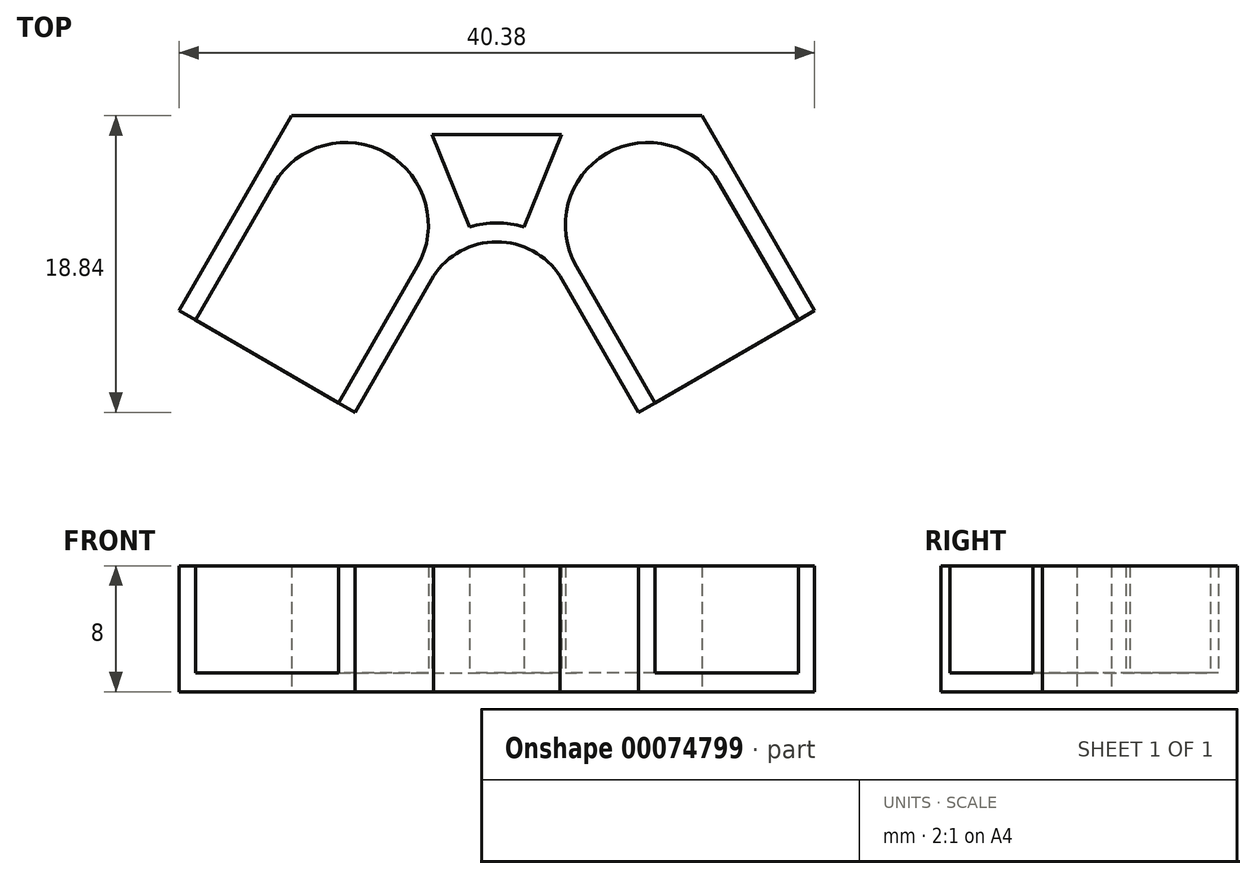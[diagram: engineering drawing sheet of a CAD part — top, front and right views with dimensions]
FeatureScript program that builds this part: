
annotation { "Feature Type Name" : "Feature", "Feature Type Description" : "" }
export const myFeature = defineFeature(function(context is Context, id is Id, definition is map)
    precondition{}
    {
        {
            var Q0;
            Q0=qCreatedBy(makeId("Top.planeOp"),FACE);
            var sketch = newSketch(context, id + "F0", { "sketchPlane" : qUnion([Q0])});
            skLineSegment(sketch, "E0", {"start": v(0, 33.26) * mm, "end": v(-19.2, 0) * mm, "construction": true});
            skLineSegment(sketch, "E1", {"start": v(-19.2, 0) * mm, "end": v(19.2, 0) * mm, "construction": true});
            skLineSegment(sketch, "E2", {"start": v(19.2, 0) * mm, "end": v(0, 33.26) * mm, "construction": true});
            skLineSegment(sketch, "E3", {"start": v(19.2, 0) * mm, "end": v(-5.05, 14) * mm, "construction": true});
            skLineSegment(sketch, "E4", {"start": v(0, 43.76) * mm, "end": v(-12.34, 22.38) * mm, "construction": true});
            skLineSegment(sketch, "E5", {"start": v(-10.05, 5.34) * mm, "end": v(-5.05, 14) * mm});
            skLineSegment(sketch, "E6", {"start": v(-14.15, 19.25) * mm, "end": v(-19.15, 10.6) * mm});
            skLineSegment(sketch, "E7", {"start": v(-10.05, 5.34) * mm, "end": v(-19.15, 10.6) * mm});
            skLineSegment(sketch, "E8.MirrorCS", {"start": v(10.05, 5.34) * mm, "end": v(19.15, 10.6) * mm});
            skLineSegment(sketch, "E9.MirrorCS", {"start": v(14.15, 19.25) * mm, "end": v(19.15, 10.6) * mm});
            skLineSegment(sketch, "E10.MirrorCS", {"start": v(10.05, 5.34) * mm, "end": v(5.05, 14) * mm});
            skLineSegment(sketch, "E11.MirrorCS", {"start": v(0, 43.76) * mm, "end": v(12.34, 22.38) * mm, "construction": true});
            skLineSegment(sketch, "E12", {"start": v(-12.63, 21.88) * mm, "end": v(12.63, 21.88) * mm, "construction": true});
            skLineSegment(sketch, "E13.0", {"start": v(-12.34, 22.38) * mm, "end": v(12.34, 22.38) * mm});
            skLineSegment(sketch, "E14", {"start": v(-5.05, 14) * mm, "end": v(-14.15, 19.25) * mm, "construction": true});
            skLineSegment(sketch, "E15", {"start": v(12.34, 22.38) * mm, "end": v(14.15, 19.25) * mm});
            skLineSegment(sketch, "E16", {"start": v(-12.34, 22.38) * mm, "end": v(-14.15, 19.25) * mm});
            skLineSegment(sketch, "E17", {"start": v(-5.05, 14) * mm, "end": v(-5.05, 14) * mm});
            skLineSegment(sketch, "E18", {"start": v(-5.05, 14) * mm, "end": v(0, 22.76) * mm, "construction": true});
            skLineSegment(sketch, "E19", {"start": v(5.05, 14) * mm, "end": v(0, 22.76) * mm, "construction": true});
            skArc(sketch, "E20", {"start": v(-14.15, 19.25) * mm, "mid": v(-6.97, 21.17) * mm, "end": v(-5.05, 14) * mm, "construction": true});
            skArc(sketch, "E21.MirrorCS", {"start": v(14.15, 19.25) * mm, "mid": v(6.97, 21.17) * mm, "end": v(5.05, 14) * mm, "construction": true});
            skArc(sketch, "E22", {"start": v(5.05, 14) * mm, "mid": v(0, 16.77) * mm, "end": v(-5.05, 14) * mm});
            skSolve(sketch);
        }
        {
            var Q0;
            Q0=qSketchRegion(id+"F0",true);
            extrude(context, id + "F1", {"entities" : qUnion([Q0]), "depth" : 1.2 * mm});
        }
        {
            var Q0;
            Q0=makeQuery(id+"F0.imprint","IMPRINT",FACE,{"disambiguationData":[TD([[makeQuery(id+"F0.imprint","IMPRINT",EDGE,{"derivedFrom":sQuery(id+"F0.wireOp",EDGE,"E5")}),1.0]])]});
            var sketch = newSketch(context, id + "F2", { "sketchPlane" : qUnion([Q0])});
            skLineSegment(sketch, "E23.3", {"start": v(-10.05, 5.34) * mm, "end": v(-5.05, 14) * mm});
            skLineSegment(sketch, "E23.4", {"start": v(-14.15, 19.25) * mm, "end": v(-19.15, 10.6) * mm});
            skLineSegment(sketch, "E23.5", {"start": v(-12.34, 22.38) * mm, "end": v(-14.15, 19.25) * mm});
            skLineSegment(sketch, "E23.6", {"start": v(-12.34, 22.38) * mm, "end": v(12.34, 22.38) * mm});
            skLineSegment(sketch, "E23.7", {"start": v(12.34, 22.38) * mm, "end": v(14.15, 19.25) * mm});
            skLineSegment(sketch, "E23.8", {"start": v(14.15, 19.25) * mm, "end": v(19.15, 10.6) * mm});
            skLineSegment(sketch, "E23.9", {"start": v(10.05, 5.34) * mm, "end": v(5.05, 14) * mm});
            skLineSegment(sketch, "E24", {"start": v(-19.15, 10.6) * mm, "end": v(-10.05, 5.34) * mm, "construction": true});
            skLineSegment(sketch, "E25.0", {"start": v(15.19, 19.85) * mm, "end": v(20.19, 11.2) * mm});
            skLineSegment(sketch, "E25.1", {"start": v(13.04, 23.58) * mm, "end": v(15.19, 19.85) * mm});
            skLineSegment(sketch, "E25.2", {"start": v(-13.04, 23.58) * mm, "end": v(13.04, 23.58) * mm});
            skLineSegment(sketch, "E25.3", {"start": v(-13.04, 23.58) * mm, "end": v(-15.19, 19.85) * mm});
            skLineSegment(sketch, "E25.4", {"start": v(-15.19, 19.85) * mm, "end": v(-20.19, 11.2) * mm});
            skLineSegment(sketch, "E25.5", {"start": v(9.01, 4.74) * mm, "end": v(4.02, 13.38) * mm});
            skArc(sketch, "E25.6", {"start": v(4.02, 13.38) * mm, "mid": v(0, 15.57) * mm, "end": v(-4.02, 13.38) * mm});
            skLineSegment(sketch, "E25.7", {"start": v(-9.01, 4.74) * mm, "end": v(-4.02, 13.38) * mm});
            skLineSegment(sketch, "E26", {"start": v(-19.15, 10.6) * mm, "end": v(-20.19, 11.2) * mm});
            skLineSegment(sketch, "E27", {"start": v(-10.05, 5.34) * mm, "end": v(-9.01, 4.74) * mm});
            skLineSegment(sketch, "E28", {"start": v(10.05, 5.34) * mm, "end": v(9.01, 4.74) * mm});
            skLineSegment(sketch, "E29", {"start": v(19.15, 10.6) * mm, "end": v(20.19, 11.2) * mm});
            skArc(sketch, "E30.0", {"start": v(5.05, 14) * mm, "mid": v(0, 16.77) * mm, "end": v(-5.05, 14) * mm});
            skSolve(sketch);
        }
        {
            var Q0;
            Q0=qSketchRegion(id+"F2",true);
            extrude(context, id + "F3", {"entities" : qUnion([Q0]), "operationType" : NewBodyOperationType.ADD, "depth" : 8 * mm});
        }
        {
            var Q0;
            Q0=makeQuery(id+"F1.opExtrude","CAP_FACE",FACE,{"disambiguationData":[OSD([sQuery(id+"F0.wireOp",EDGE,"E5"),sQuery(id+"F0.wireOp",EDGE,"E6"),sQuery(id+"F0.wireOp",EDGE,"E7"),sQuery(id+"F0.wireOp",EDGE,"E8.MirrorCS"),sQuery(id+"F0.wireOp",EDGE,"E9.MirrorCS"),sQuery(id+"F0.wireOp",EDGE,"E10.MirrorCS"),sQuery(id+"F0.wireOp",EDGE,"E13.0"),sQuery(id+"F0.wireOp",EDGE,"E15"),sQuery(id+"F0.wireOp",EDGE,"E16"),sQuery(id+"F0.wireOp",EDGE,"E22")])],"isStart":false});
            var sketch = newSketch(context, id + "F4", { "sketchPlane" : qUnion([Q0])});
            skLineSegment(sketch, "E31.0", {"start": v(-12.34, 22.38) * mm, "end": v(-14.15, 19.25) * mm});
            skArc(sketch, "E31.1", {"start": v(-14.15, 19.25) * mm, "mid": v(-6.97, 21.17) * mm, "end": v(-5.05, 14) * mm});
            skArc(sketch, "E31.2", {"start": v(5.05, 14) * mm, "mid": v(3.61, 15.56) * mm, "end": v(1.73, 16.51) * mm});
            skArc(sketch, "E31.3", {"start": v(14.15, 19.25) * mm, "mid": v(6.97, 21.17) * mm, "end": v(5.05, 14) * mm});
            skLineSegment(sketch, "E31.4", {"start": v(12.34, 22.38) * mm, "end": v(14.15, 19.25) * mm});
            skLineSegment(sketch, "E31.5", {"start": v(-12.34, 22.38) * mm, "end": v(-4.11, 22.38) * mm});
            skLineSegment(sketch, "E32", {"start": v(-6.27, 22.38) * mm, "end": v(-3.52, 15.62) * mm, "construction": true});
            skLineSegment(sketch, "E33.0", {"start": v(-4.11, 22.38) * mm, "end": v(-1.73, 16.51) * mm});
            skLineSegment(sketch, "E34.MirrorCS", {"start": v(4.11, 22.38) * mm, "end": v(1.73, 16.51) * mm});
            skLineSegment(sketch, "E35.MirrorCS", {"start": v(6.27, 22.38) * mm, "end": v(3.52, 15.62) * mm, "construction": true});
            skLineSegment(sketch, "E36.trimOffspring", {"start": v(4.11, 22.38) * mm, "end": v(12.34, 22.38) * mm});
            skArc(sketch, "E37.trimOffspring", {"start": v(-1.73, 16.51) * mm, "mid": v(-3.61, 15.56) * mm, "end": v(-5.05, 14) * mm});
            skSolve(sketch);
        }
        {
            var Q0;
            Q0=qSketchRegion(id+"F4",true);
            var Q1;
            Q1=makeQuery(id+"F3.opExtrude","CAP_FACE",FACE,{"disambiguationData":[OSD([sQuery(id+"F2.wireOp",EDGE,"E23.4"),sQuery(id+"F2.wireOp",EDGE,"E23.5"),sQuery(id+"F2.wireOp",EDGE,"E23.6"),sQuery(id+"F2.wireOp",EDGE,"E23.7"),sQuery(id+"F2.wireOp",EDGE,"E23.8"),sQuery(id+"F2.wireOp",EDGE,"E25.0"),sQuery(id+"F2.wireOp",EDGE,"E25.1"),sQuery(id+"F2.wireOp",EDGE,"E25.2"),sQuery(id+"F2.wireOp",EDGE,"E25.3"),sQuery(id+"F2.wireOp",EDGE,"E25.4"),sQuery(id+"F2.wireOp",EDGE,"E26"),sQuery(id+"F2.wireOp",EDGE,"E29")])],"isStart":false});
            extrude(context, id + "F5", {"entities" : qUnion([Q0]), "operationType" : NewBodyOperationType.ADD, "endBound" : BoundingType.UP_TO_SURFACE, "endBoundEntityFace" : qUnion([Q1]), "depth" : 8.8 * mm});
        }
    });
